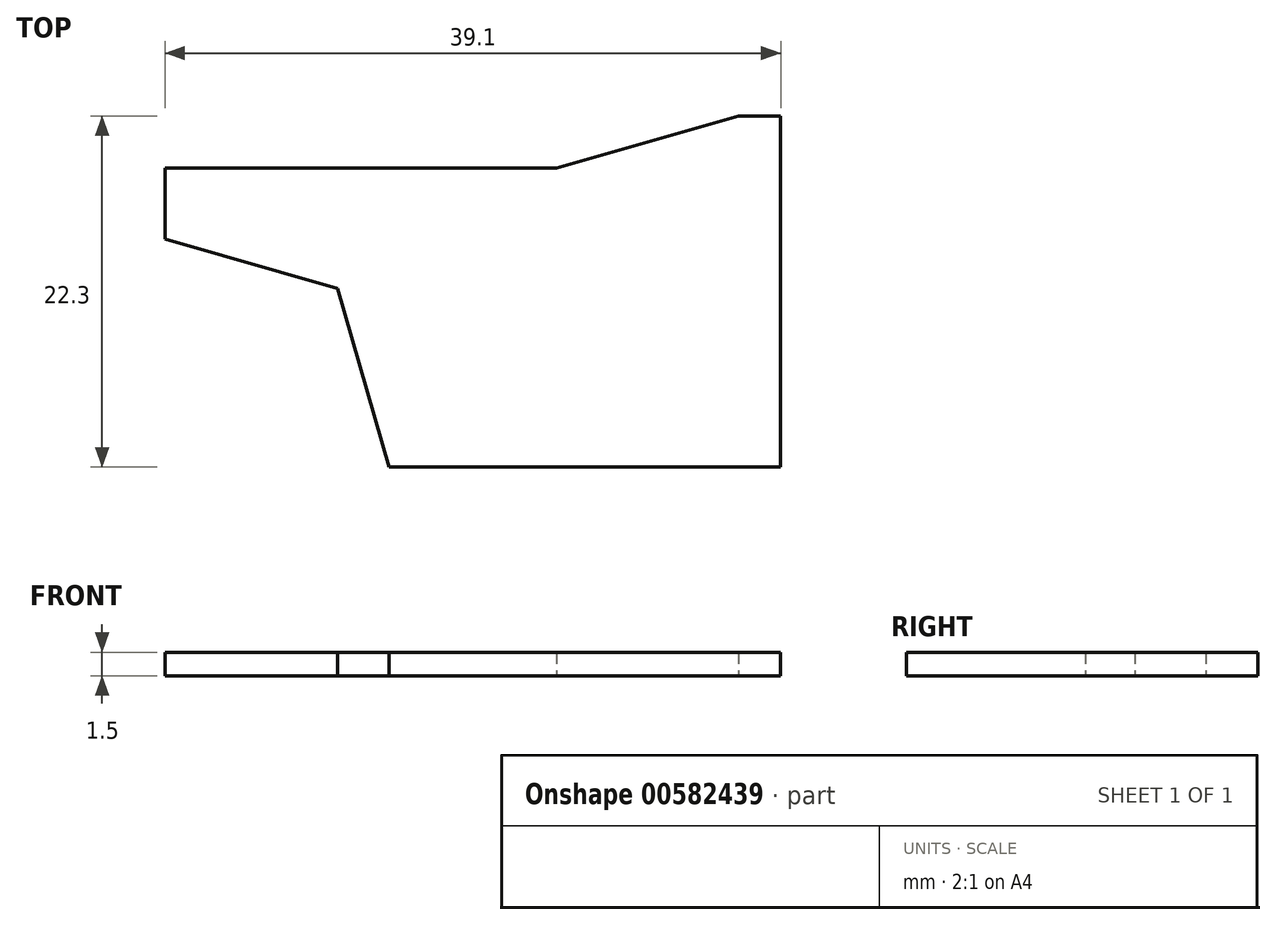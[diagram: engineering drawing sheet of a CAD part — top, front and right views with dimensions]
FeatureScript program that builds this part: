
annotation { "Feature Type Name" : "Feature", "Feature Type Description" : "" }
export const myFeature = defineFeature(function(context is Context, id is Id, definition is map)
    precondition{}
    {
        {
            var Q0;
            Q0=qCreatedBy(makeId("Top.planeOp"),FACE);
            var sketch = newSketch(context, id + "F0", { "sketchPlane" : qUnion([Q0])});
            skLineSegment(sketch, "E0", {"start": v(-138.28, 19.94) * mm, "end": v(-113.4, 19.94) * mm});
            skLineSegment(sketch, "E1", {"start": v(-113.4, 19.94) * mm, "end": v(-101.88, 23.24) * mm});
            skLineSegment(sketch, "E2", {"start": v(-101.88, 23.24) * mm, "end": v(-99.18, 23.24) * mm});
            skLineSegment(sketch, "E3", {"start": v(-99.18, 23.24) * mm, "end": v(-99.18, 0.94) * mm});
            skLineSegment(sketch, "E4", {"start": v(-99.18, 0.94) * mm, "end": v(-124.08, 0.94) * mm});
            skLineSegment(sketch, "E5", {"start": v(-124.08, 0.94) * mm, "end": v(-127.33, 12.3) * mm});
            skLineSegment(sketch, "E6", {"start": v(-127.33, 12.3) * mm, "end": v(-138.28, 15.44) * mm});
            skLineSegment(sketch, "E7", {"start": v(-138.28, 15.44) * mm, "end": v(-138.28, 19.94) * mm});
            skSolve(sketch);
        }
        {
            var Q0;
            Q0=makeQuery(id+"F0.imprint","IMPRINT",FACE,{"disambiguationData":[TD([[makeQuery(id+"F0.imprint","IMPRINT",EDGE,{"derivedFrom":sQuery(id+"F0.wireOp",EDGE,"E0")}),-1.0]])]});
            extrude(context, id + "F1", {"entities" : qUnion([Q0]), "depth" : 1.5 * mm, "offsetDistance" : 25 * mm});
        }
    });
